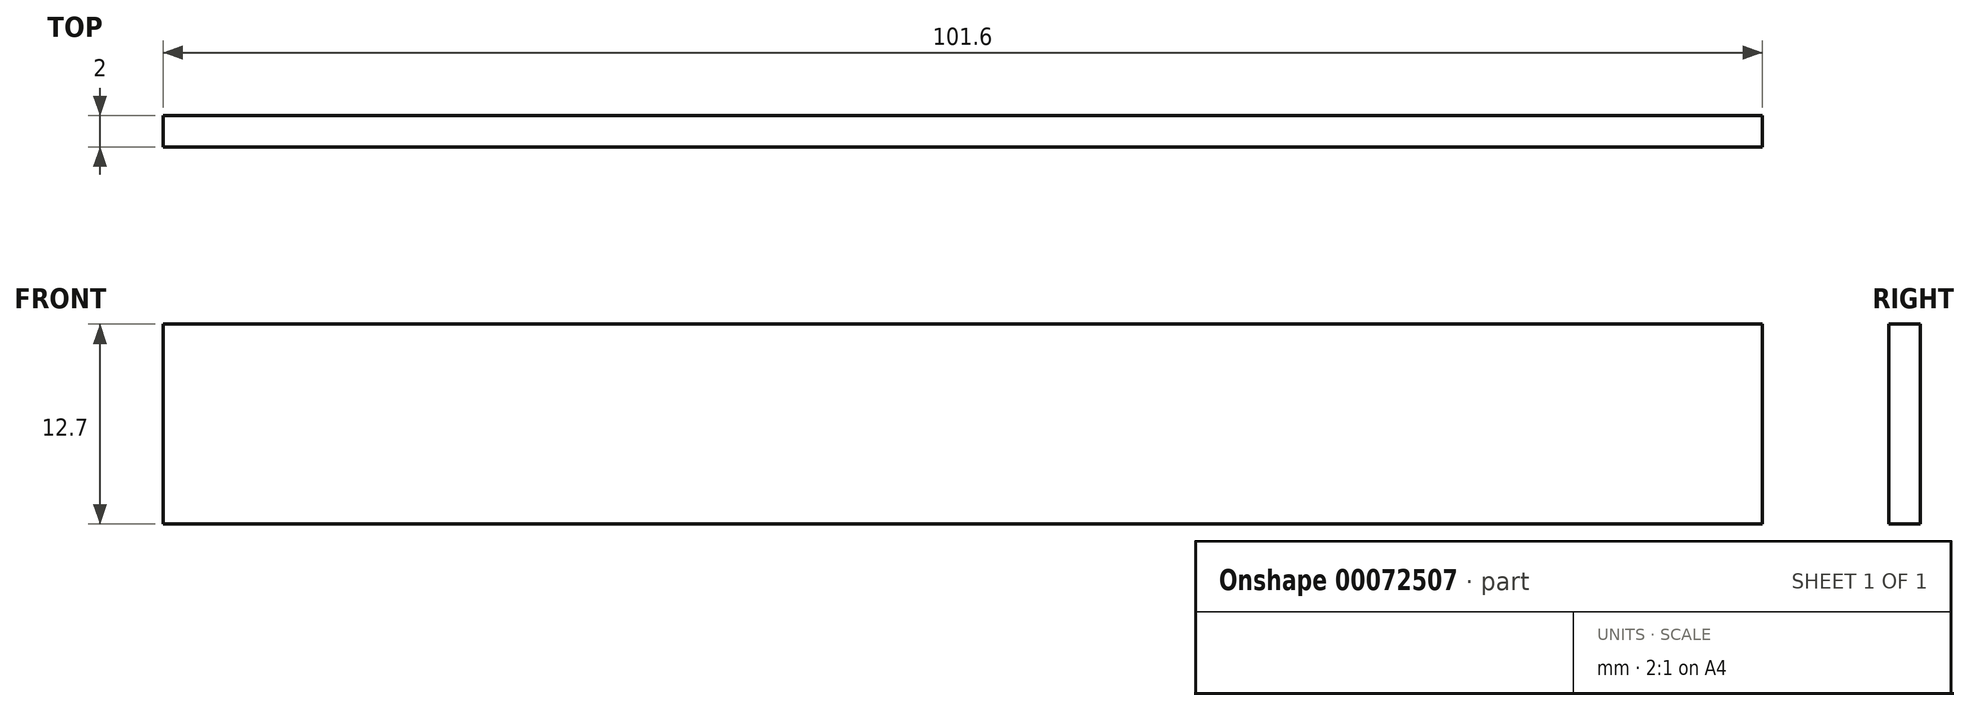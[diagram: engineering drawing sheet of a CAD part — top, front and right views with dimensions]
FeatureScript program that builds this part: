
annotation { "Feature Type Name" : "Feature", "Feature Type Description" : "" }
export const myFeature = defineFeature(function(context is Context, id is Id, definition is map)
    precondition{}
    {
        {
            var Q0;
            Q0=qCreatedBy(makeId("Front.planeOp"),FACE);
            var sketch = newSketch(context, id + "F0", { "sketchPlane" : qUnion([Q0])});
            skLineSegment(sketch, "E0.rect.bottom", {"start": v(-50.8, 6.35) * mm, "end": v(50.8, 6.35) * mm});
            skLineSegment(sketch, "E0.rect.top", {"start": v(-50.8, -6.35) * mm, "end": v(50.8, -6.35) * mm});
            skLineSegment(sketch, "E0.rect.left", {"start": v(-50.8, 6.35) * mm, "end": v(-50.8, -6.35) * mm});
            skLineSegment(sketch, "E0.rect.right", {"start": v(50.8, 6.35) * mm, "end": v(50.8, -6.35) * mm});
            skPoint(sketch, "E0.rect.middle", {"position": v(0, 0) * mm});
            skSolve(sketch);
        }
        {
            var Q0;
            Q0 = qSketchRegion(id + "F0", true);
            extrude(context, id + "F1", {"entities" : qUnion([Q0]), "endBound" : BoundingType.SYMMETRIC, "depth" : 2 * mm});
        }
    });
